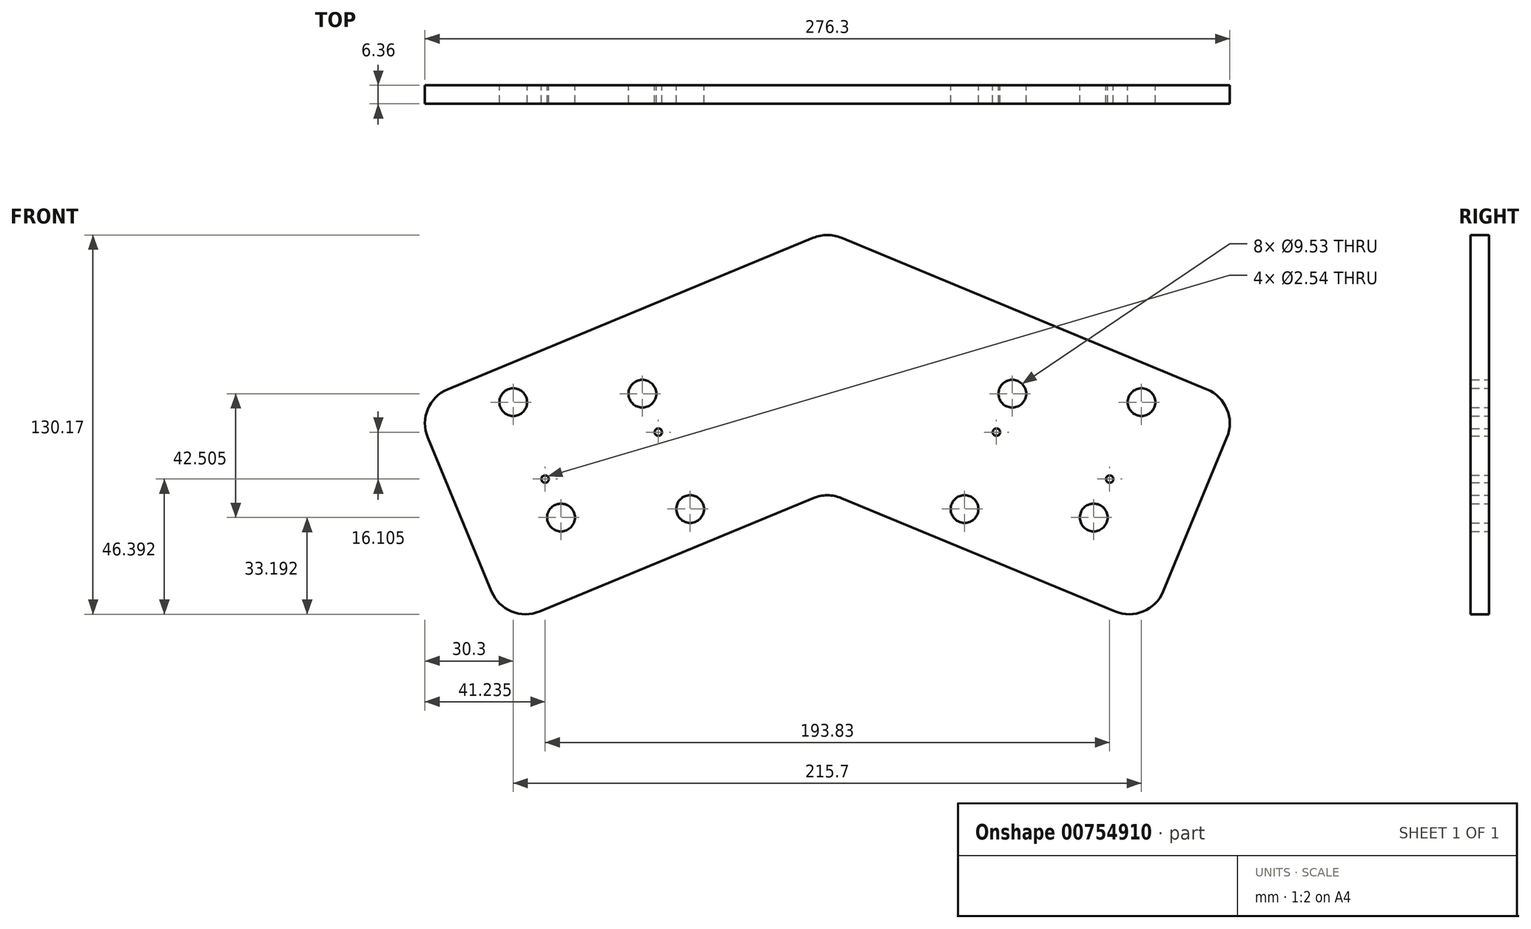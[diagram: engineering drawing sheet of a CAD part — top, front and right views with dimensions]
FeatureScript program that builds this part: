
annotation { "Feature Type Name" : "Feature", "Feature Type Description" : "" }
export const myFeature = defineFeature(function(context is Context, id is Id, definition is map)
    precondition{}
    {
        {
            var Q0;
            Q0=qCreatedBy(makeId("Front.planeOp"),FACE);
            var sketch = newSketch(context, id + "F0", { "sketchPlane" : qUnion([Q0])});
            skLineSegment(sketch, "E0", {"start": v(0, 0) * mm, "end": v(-110.45, -45.75) * mm});
            skLineSegment(sketch, "E1", {"start": v(0, 0) * mm, "end": v(0, 89.35) * mm});
            skLineSegment(sketch, "E2", {"start": v(-110.45, -45.75) * mm, "end": v(-142.04, 30.52) * mm});
            skLineSegment(sketch, "E3", {"start": v(-142.04, 30.52) * mm, "end": v(0, 89.35) * mm});
            skPoint(sketch, "E4", {"position": v(-15.88, 93.09) * mm});
            skPoint(sketch, "E5", {"position": v(-15.88, -16.89) * mm});
            skLineSegment(sketch, "E6.MirrorCS", {"start": v(0, 0) * mm, "end": v(110.45, -45.75) * mm});
            skPoint(sketch, "E7.MirrorP", {"position": v(15.88, -16.89) * mm});
            skLineSegment(sketch, "E8.MirrorCS", {"start": v(110.45, -45.75) * mm, "end": v(142.04, 30.52) * mm});
            skLineSegment(sketch, "E9.MirrorCS", {"start": v(142.04, 30.52) * mm, "end": v(0, 89.35) * mm});
            skPoint(sketch, "E10.MirrorP", {"position": v(15.88, 93.09) * mm});
            skLineSegment(sketch, "E11", {"start": v(-15.87, -16.89) * mm, "end": v(-45.04, 53.51) * mm, "construction": true});
            skLineSegment(sketch, "E12", {"start": v(-15.88, 93.09) * mm, "end": v(13.29, 22.69) * mm, "construction": true});
            skCircle(sketch, "E13", {"center": v(-91.45, -8.67) * mm, "radius": 4.76 * mm});
            skLineSegment(sketch, "E14", {"start": v(-91.45, -8.67) * mm, "end": v(-112.71, 42.67) * mm, "construction": true});
            skCircle(sketch, "E15", {"center": v(-107.85, 30.93) * mm, "radius": 4.76 * mm});
            skCircle(sketch, "E16.MirrorC", {"center": v(91.45, -8.67) * mm, "radius": 4.76 * mm});
            skCircle(sketch, "E17.MirrorC", {"center": v(107.85, 30.93) * mm, "radius": 4.76 * mm});
            skCircle(sketch, "E18", {"center": v(-63.5, 33.84) * mm, "radius": 4.76 * mm});
            skLineSegment(sketch, "E19", {"start": v(-63.5, 33.84) * mm, "end": v(-42.24, -17.5) * mm});
            skCircle(sketch, "E20", {"center": v(-47.1, -5.76) * mm, "radius": 4.76 * mm});
            skCircle(sketch, "E21.MirrorC", {"center": v(47.1, -5.76) * mm, "radius": 4.76 * mm});
            skCircle(sketch, "E22.MirrorC", {"center": v(63.5, 33.84) * mm, "radius": 4.76 * mm});
            skCircle(sketch, "E23", {"center": v(-58.03, 20.64) * mm, "radius": 1.27 * mm});
            skCircle(sketch, "E24", {"center": v(-96.91, 4.53) * mm, "radius": 1.27 * mm});
            skCircle(sketch, "E25.MirrorC", {"center": v(58.03, 20.64) * mm, "radius": 1.27 * mm});
            skCircle(sketch, "E26.MirrorC", {"center": v(96.91, 4.53) * mm, "radius": 1.27 * mm});
            skPoint(sketch, "E27", {"position": v(-102.08, 17) * mm});
            skSolve(sketch);
        }
        {
            var Q0;
            Q0=qSketchRegion(id+"F0",true);
            extrude(context, id + "F1", {"entities" : qUnion([Q0]), "endBound" : BoundingType.SYMMETRIC, "depth" : 6.35 * mm, "offsetDistance" : 25.4 * mm});
        }
        {
            var Q0;
            Q0=makeQuery(id+"F1.opExtrude","SWEPT_EDGE",EDGE,{"disambiguationData":[OSD([sQuery(id+"F0.wireOp",EDGE,"E2"),sQuery(id+"F0.wireOp",EDGE,"E3")])]});
            var Q1;
            Q1=makeQuery(id+"F1.opExtrude","SWEPT_EDGE",EDGE,{"disambiguationData":[OSD([sQuery(id+"F0.wireOp",EDGE,"E3"),sQuery(id+"F0.wireOp",EDGE,"E1"),sQuery(id+"F0.wireOp",EDGE,"E9.MirrorCS")])]});
            var Q2;
            Q2=makeQuery(id+"F1.opExtrude","SWEPT_EDGE",EDGE,{"disambiguationData":[OSD([sQuery(id+"F0.wireOp",EDGE,"E0"),sQuery(id+"F0.wireOp",EDGE,"E6.MirrorCS"),sQuery(id+"F0.wireOp",EDGE,"E1")])]});
            var Q3;
            Q3=makeQuery(id+"F1.opExtrude","SWEPT_EDGE",EDGE,{"disambiguationData":[OSD([sQuery(id+"F0.wireOp",EDGE,"E6.MirrorCS"),sQuery(id+"F0.wireOp",EDGE,"E8.MirrorCS")])]});
            var Q4;
            Q4=makeQuery(id+"F1.opExtrude","SWEPT_EDGE",EDGE,{"disambiguationData":[OSD([sQuery(id+"F0.wireOp",EDGE,"E8.MirrorCS"),sQuery(id+"F0.wireOp",EDGE,"E9.MirrorCS")])]});
            var Q5;
            Q5=makeQuery(id+"F1.opExtrude","SWEPT_EDGE",EDGE,{"disambiguationData":[OSD([sQuery(id+"F0.wireOp",EDGE,"E0"),sQuery(id+"F0.wireOp",EDGE,"E2")])]});
            fillet(context, id + "F2", {"entities" : qUnion([Q0, Q1, Q2, Q3, Q4, Q5]), "radius" : 12.7 * mm, "tangentPropagation" : true, "allowEdgeOverflow" : false});
        }
    });
